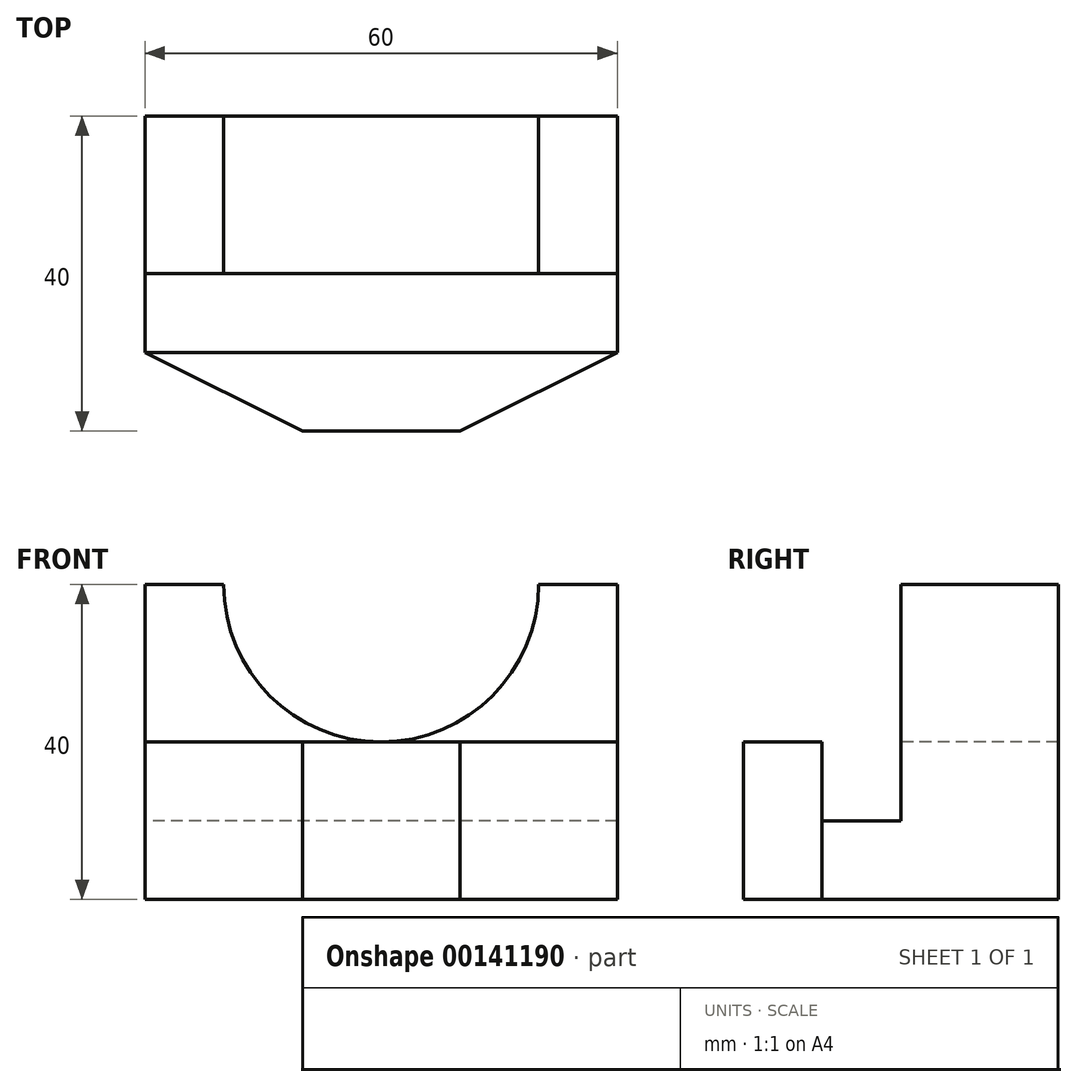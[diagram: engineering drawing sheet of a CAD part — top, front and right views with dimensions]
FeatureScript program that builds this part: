
annotation { "Feature Type Name" : "Feature", "Feature Type Description" : "" }
export const myFeature = defineFeature(function(context is Context, id is Id, definition is map)
    precondition{}
    {
        {
            var Q0;
            Q0=qCreatedBy(makeId("Right.planeOp"),FACE);
            var sketch = newSketch(context, id + "F0", { "sketchPlane" : qUnion([Q0])});
            skLineSegment(sketch, "E0", {"start": v(0, 0) * mm, "end": v(0, 20) * mm});
            skLineSegment(sketch, "E1", {"start": v(0, 20) * mm, "end": v(10, 20) * mm});
            skLineSegment(sketch, "E2", {"start": v(10, 20) * mm, "end": v(10, 0) * mm});
            skLineSegment(sketch, "E3", {"start": v(10, 0) * mm, "end": v(0, 0) * mm});
            skLineSegment(sketch, "E4", {"start": v(10, 10) * mm, "end": v(20, 10) * mm});
            skLineSegment(sketch, "E5", {"start": v(20, 10) * mm, "end": v(20, 40) * mm});
            skLineSegment(sketch, "E6", {"start": v(20, 40) * mm, "end": v(40, 40) * mm});
            skLineSegment(sketch, "E7", {"start": v(40, 40) * mm, "end": v(40, 0) * mm});
            skLineSegment(sketch, "E8", {"start": v(40, 0) * mm, "end": v(10, 0) * mm});
            skSolve(sketch);
        }
        {
            var Q0;
            Q0 = qSketchRegion(id + "F0", true);
            extrude(context, id + "F1", {"entities" : qUnion([Q0]), "endBound" : BoundingType.SYMMETRIC, "depth" : 60 * mm});
        }
        {
            var Q0;
            Q0=makeQuery(id+"F1.opExtrude","SWEPT_FACE",FACE,{"disambiguationData":[OSD([sQuery(id+"F0.wireOp",EDGE,"E1")])]});
            var sketch = newSketch(context, id + "F2", { "sketchPlane" : qUnion([Q0])});
            skLineSegment(sketch, "E9", {"start": v(30, 10) * mm, "end": v(-30, 10) * mm});
            skLineSegment(sketch, "E10", {"start": v(0, 0) * mm, "end": v(-10, 0) * mm});
            skLineSegment(sketch, "E11", {"start": v(0, 0) * mm, "end": v(10, 0) * mm});
            skLineSegment(sketch, "E12", {"start": v(-10, 0) * mm, "end": v(-30, 10) * mm});
            skLineSegment(sketch, "E13", {"start": v(10, 0) * mm, "end": v(30, 10) * mm});
            skSolve(sketch);
        }
        {
            var Q0;
            {var subQ0=sQuery(id+"F2.wireOp",EDGE,"E12");Q0=makeQuery(id+"F2.imprint","IMPRINT",FACE,{"disambiguationData":[TD([[makeQuery(id+"F2.imprint","IMPRINT",EDGE,{"derivedFrom":subQ0}),1.0]])]});}
            var Q1;
            {var subQ0=sQuery(id+"F2.wireOp",EDGE,"E13");Q1=makeQuery(id+"F2.imprint","IMPRINT",FACE,{"disambiguationData":[TD([[makeQuery(id+"F2.imprint","IMPRINT",EDGE,{"derivedFrom":subQ0}),-1.0]])]});}
            extrude(context, id + "F3", {"entities" : qUnion([Q0, Q1]), "operationType" : NewBodyOperationType.REMOVE, "endBound" : BoundingType.THROUGH_ALL, "oppositeDirection" : true, "depth" : 25 * mm});
        }
        {
            var Q0;
            Q0=makeQuery(id+"F1.opExtrude","SWEPT_FACE",FACE,{"disambiguationData":[OSD([sQuery(id+"F0.wireOp",EDGE,"E5")])]});
            var sketch = newSketch(context, id + "F4", { "sketchPlane" : qUnion([Q0])});
            skLineSegment(sketch, "E14", {"start": v(-30, 40) * mm, "end": v(-20, 40) * mm});
            skLineSegment(sketch, "E15", {"start": v(30, 40) * mm, "end": v(20, 40) * mm});
            skArc(sketch, "E16", {"start": v(-20, 40) * mm, "mid": v(0, 20) * mm, "end": v(20, 40) * mm});
            skSolve(sketch);
        }
        {
            var Q0;
            {var subQ0=sQuery(id+"F4.wireOp",EDGE,"E16");Q0=makeQuery(id+"F4.imprint","IMPRINT",FACE,{"disambiguationData":[TD([[makeQuery(id+"F4.imprint","IMPRINT",EDGE,{"derivedFrom":subQ0}),1.0]])]});}
            extrude(context, id + "F5", {"entities" : qUnion([Q0]), "operationType" : NewBodyOperationType.REMOVE, "endBound" : BoundingType.THROUGH_ALL, "oppositeDirection" : true, "depth" : 25 * mm});
        }
    });
